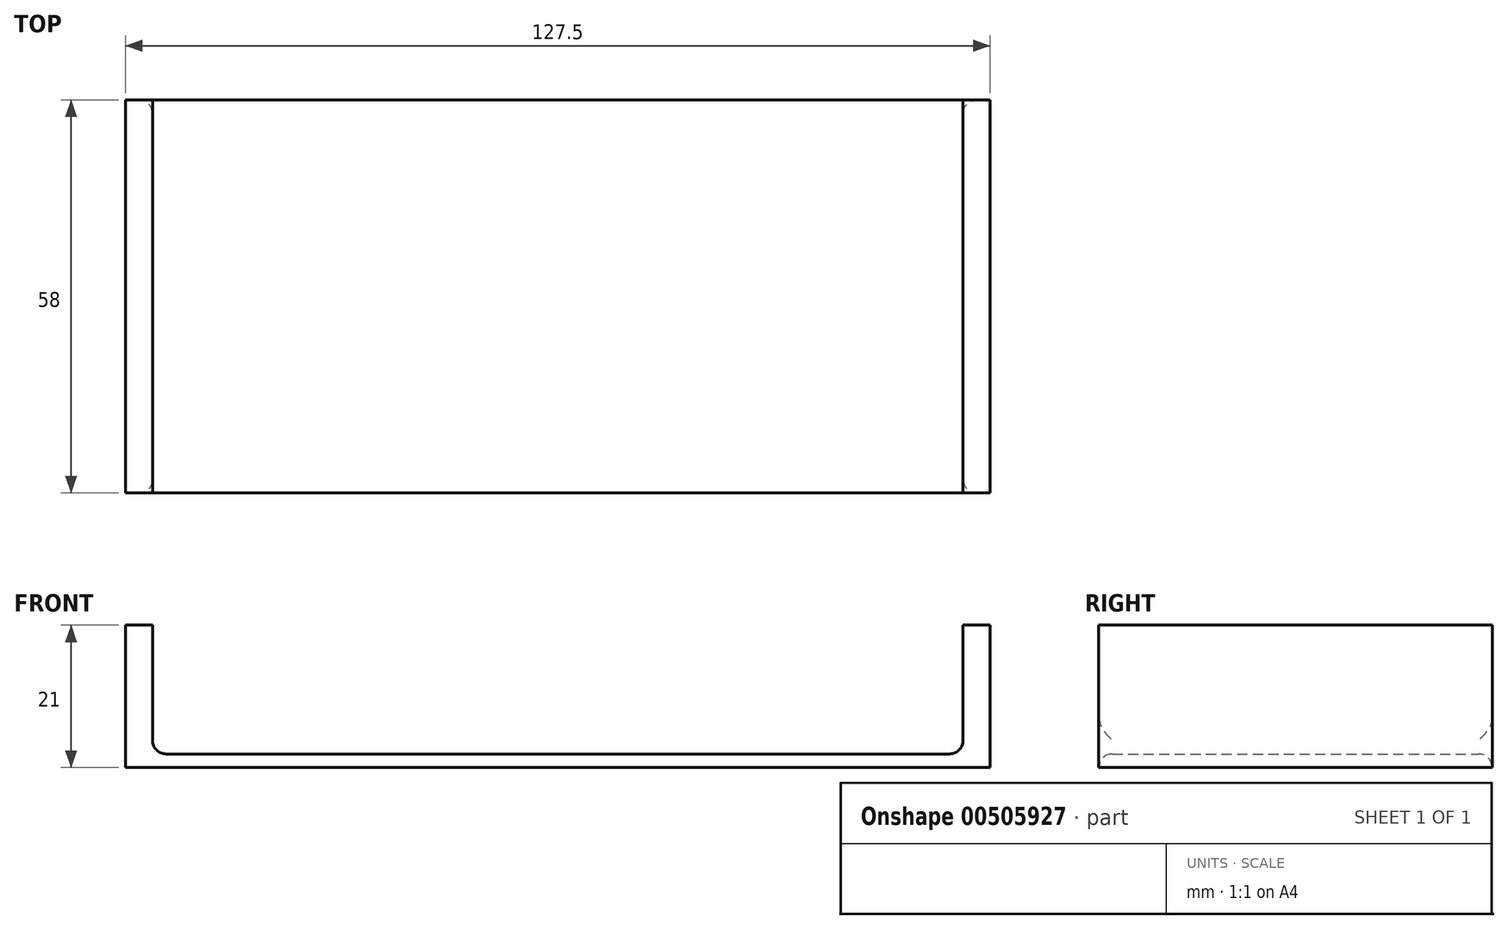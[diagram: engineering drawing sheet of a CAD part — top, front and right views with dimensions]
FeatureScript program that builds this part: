
annotation { "Feature Type Name" : "Feature", "Feature Type Description" : "" }
export const myFeature = defineFeature(function(context is Context, id is Id, definition is map)
    precondition{}
    {
        {
            var Q0;
            Q0=qCreatedBy(makeId("Front.planeOp"),FACE);
            var sketch = newSketch(context, id + "F0", { "sketchPlane" : qUnion([Q0])});
            skLineSegment(sketch, "E0", {"start": v(-49.15, 3.83) * mm, "end": v(70.35, 3.83) * mm});
            skLineSegment(sketch, "E1.0", {"start": v(-53.15, 1.83) * mm, "end": v(-53.15, 22.83) * mm});
            skLineSegment(sketch, "E1.1", {"start": v(-53.15, 1.83) * mm, "end": v(74.35, 1.83) * mm});
            skLineSegment(sketch, "E1.2", {"start": v(74.35, 1.83) * mm, "end": v(74.35, 22.83) * mm});
            skLineSegment(sketch, "E2", {"start": v(-53.15, 22.83) * mm, "end": v(-49.15, 22.83) * mm});
            skLineSegment(sketch, "E3", {"start": v(74.35, 22.83) * mm, "end": v(74.35, 22.83) * mm});
            skLineSegment(sketch, "E4", {"start": v(74.35, 22.83) * mm, "end": v(70.35, 22.83) * mm});
            skLineSegment(sketch, "E5", {"start": v(70.35, 22.83) * mm, "end": v(70.35, 3.83) * mm});
            skLineSegment(sketch, "E6", {"start": v(-49.15, 22.83) * mm, "end": v(-49.15, 3.83) * mm});
            skPoint(sketch, "E7.start.orphan", {"position": v(-51.15, 3.83) * mm});
            skSolve(sketch);
        }
        {
            var Q0;
            Q0 = qSketchRegion(id + "F0", true);
            extrude(context, id + "F1", {"entities" : qUnion([Q0]), "depth" : 58 * mm});
        }
        {
            var Q0;
            Q0=makeQuery(id+"F1.opExtrude","SWEPT_FACE",FACE,{"disambiguationData":[OSD([sQuery(id+"F0.wireOp",EDGE,"E0")])]});
            fillet(context, id + "F2", {"entities" : qUnion([Q0]), "radius" : 2 * mm, "tangentPropagation" : true, "allowEdgeOverflow" : false});
        }
    });
